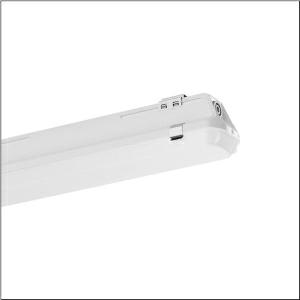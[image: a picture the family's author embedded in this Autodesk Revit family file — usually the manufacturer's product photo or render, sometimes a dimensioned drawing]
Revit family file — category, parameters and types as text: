
# Revit family: monsun_r__11_51fp12mp4b0q_eb41
name_source: partatom
category: Lighting Fixtures
units: mm (PartAtom-declared; Revit-internal decimal feet)

## family parameters
Cut with Voids When Loaded = No
Host = Face
Light Source = No
Part Type = Normal
Room Calculation Point = No
Round Connector Dimension = Use Diameter
Shared = No

## types (1)
- --- (1 x LED, 11850 lm, 66.2 W, 4000K)
    Apparent Load = 66 VA
    CIE Flux Codes = 62 86 96 97 100
    Color Rendering = 80
    Color Temperature = 4000K
    Default Elevation = 1800 mm
    Description = Monsun® 11, damp-proof luminaire, chain hanger, primary light control with lens, primary optical cover: enclosure, of PMMA, light emission: direct distribution, primary light characteristic: symmetric, installation type: suspended mounting, surface-mounted, horizontal mounting, vertical mounting, LED, rated luminous flux: 11.850lm, luminous efficacy: 179lm/W, light colour: 840, colour temperature: 4000K, control gear: ECG, with terminal, 3-pole, max. 2.5mm², mains connection: 220..240V, AC, 50/60Hz, rated input power: 66W, luminaire housing, of glass-fibre reinforced polyester, uncoated, bright grey, incl. chain hanger, length: 1.590mm, width: 90mm, height: 88mm, clip for enclosure, of stainless steel (V2A), ceiling mounting element, of stainless steel (V2A), chain hanger, of stainless steel (V2A), protection rating (complete): IP66, insulation class (complete): insulation class I (protective earthing), certification: CE, ENEC, VDE, UKCA, protection symbol: D, impact resistance: IK04, permissible operating ambient temperature: -35..+35°C, standard: EN 50419, EN 60598-2-1, no direct snow, no direct sun, no direct rain, for indoor or canopied outdoor use, corresponds to IFS (International Featured Standards) requirements for safety and quality in the food industry, contact your sales advisor before using the luminaires in applications with unclear chemical exposure, large temperature fluctuations or condensation-forming humidity, LABS conformity tested according to VDMA 24364:2018-05, packaging unit: 1 piece
    Height = 89 mm
    Lamp = 1 x LED
    Lamp Light Flux = 11850 lm
    Lamp Power = 66.2 W
    Lamp count = 1
    Length = 1590 mm
    Luminous efficacy = 179 lm/W
    Manufacturer = Siteco
    ModVariant = No
    Model = 51FP12MP4B0Q
    Mounting Place = Ceiling
    Mounting Type = Surface mounted
    Number of Poles = 1
    OnlyDefault = Yes
    Power Factor = 1
    Product Name = Monsun® 11
    Product group = damp-proof luminaire
    ProductGroupID = 301
    Protection Class = Protection class I
    Protection Degree = IP 66
    RLX_Detail_Level = 1
    RLX_Emergency_Light_Flux = 0 lm
    RLX_Emergency_Type = 0
    RLX_Emergency_Type_DB = No
    RlxData = <blob elided: 89713 chars, md5=c3d8742e>
    Socket = socket
    Standby Power = 0 W
    System Light Flux = 11850 lm
    System Power = 66 W
    Type Comments = factory setting: luminous flux: 100 % | (A | C | E) | 155 mA
    Type Image = l_1004748.jpg
    URL = http://relux.com
    VarID = @adj_157045
    Voltage = 0 V
    Weight = 0.00 kg
    Width = 90 mm

## geometry (parser evidence)
native form markers: Blend x4, Sweep x9
no freeform markers — native parametric forms only
